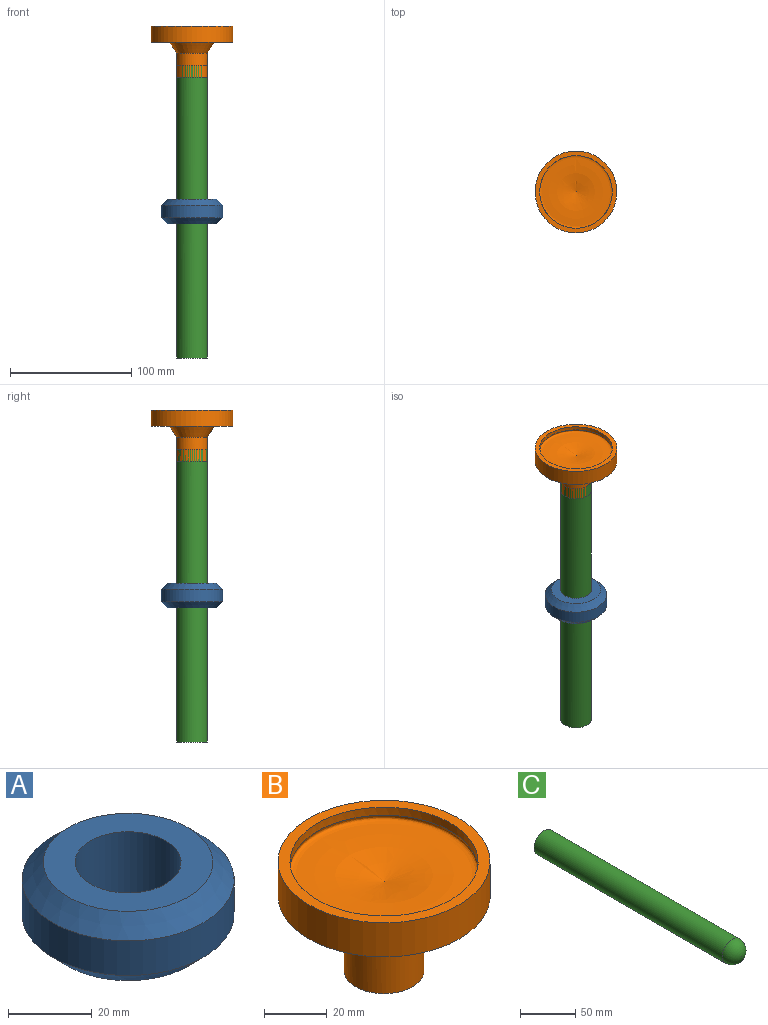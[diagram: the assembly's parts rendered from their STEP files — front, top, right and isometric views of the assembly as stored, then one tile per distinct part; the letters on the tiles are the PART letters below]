
ASSEMBLY  parts=3 mates=2
PART A: 6 faces, bbox 50.8x50.8x20.3 mm
  f0: cylinder r=12.7mm len=25.4mm, axis (0,0,-1), area 1621.5mm2, adj f2,f3
  f1: cylinder r=25.4mm len=50.8mm, axis (0,0,-1), area 1621.5mm2, adj f4,f5
  f2: plane 40.64x40.64mm, normal (0,0,1), area 790.5mm2, adj f0,f5
  f3: plane 40.64x40.64mm, normal (0,0,-1), area 790.5mm2, adj f0,f4
  f4: cone r=25.4mm half-angle=45deg, axis (0,0,1), area 1031.9mm2, adj f1,f3
  f5: cone r=20.32mm half-angle=45deg, axis (0,0,-1), area 1031.9mm2, adj f1,f2
PART B: 8 faces, bbox 67.5x67.5x42.5 mm
  f0: revolved ~25.4x25.4mm, area 676.5mm2, adj f1
  f1: cylinder r=12.7mm len=25.4mm, axis (0,0,1), area 1608mm2, adj f0,f2
  f2: cone r=12.7mm half-angle=32.9deg, axis (0,0,1), area 1054.4mm2, adj f1,f3
  f3: plane 67.48x67.48mm, normal (0,0,-1), area 2497.9mm2, adj f2,f4
  f4: cylinder r=33.74mm len=67.48mm, axis (0,0,1), area 2821.7mm2, adj f3,f5
  f5: plane 67.48x67.48mm, normal (0,0,1), area 760.8mm2, adj f4,f6
  f6: cylinder r=29.94mm len=59.88mm, axis (0,0,1), area 585.3mm2, adj f5,f7
  f7: revolved ~60.22x60.22mm, area 3117.1mm2, adj f6
PART C: 3 faces, bbox 25.4x254x25.4 mm
  f0: cylinder r=12.7mm len=241.3mm, axis (0,1,0), area 19254.9mm2, adj f1,f2
  f1: plane 25.4x25.4mm, normal (0,1,0), area 506.7mm2, adj f0
  f2: sphere r=12.7mm, area 1013.4mm2, adj f0
PLACE A at identity
PLACE B t=(0,0,120.73)mm
PLACE C rot(axis=(-1,0,0),90deg) t=(0,0,-110.49)mm
MATE slider C.f0 <-> A.f0  axis (0,0,-1) through (0,0,10.16)mm
MATE fastened B.f1 <-> C.f0  axis (0,0,1) through (0,0,130.81)mm
